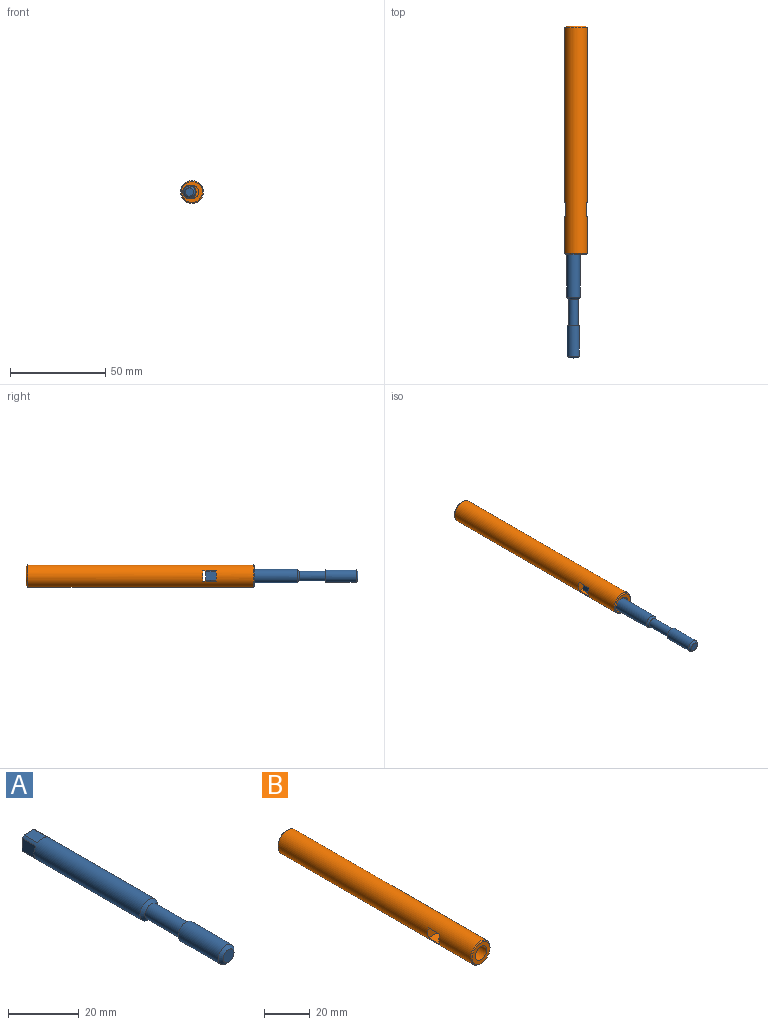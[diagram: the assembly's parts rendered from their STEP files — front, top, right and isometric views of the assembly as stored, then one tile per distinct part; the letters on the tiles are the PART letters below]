
ASSEMBLY  parts=2 mates=1
PART A: 16 faces, bbox 7x80x7 mm
  f0: cylinder r=3.5mm len=48mm, axis (0,1,0), area 958.9mm2, adj f1,f3,f8,f9,f10,f11,f12,f13
  f1: plane 5.82x5.5mm, normal (0,1,0), area 30.9mm2, adj f0,f9,f11,f13,f15
  f2: cylinder r=2.5mm len=14mm, axis (0,-1,0), area 219.9mm2, adj f3,f5
  f3: cone r=1.5mm half-angle=45deg, axis (0,1,0), area 26.7mm2, adj f0,f2
  f4: cylinder r=3.17mm len=16mm, axis (0,-1,0), area 319.2mm2, adj f5,f7
  f5: plane 6.35x6.35mm, normal (0,1,0), area 12mm2, adj f2,f4
  f6: plane 4.35x4.35mm, normal (0,-1,0), area 14.9mm2, adj f7
  f7: cone r=2.17mm half-angle=45deg, axis (0,1,0), area 23.8mm2, adj f4,f6
  f8: plane 3.89x0.59mm, normal (0,1,0), area 1.6mm2, adj f0,f9
  f9: plane 5.5x3.89mm, normal (0,0,1), area 21.4mm2, adj f0,f1,f8
  f10: plane 4.33x0.75mm, normal (0,1,0), area 2.2mm2, adj f0,f11
  f11: plane 5.5x4.33mm, normal (-1,0,0), area 23.8mm2, adj f0,f1,f10
  f12: plane 3.89x0.59mm, normal (0,1,0), area 1.6mm2, adj f0,f13
  f13: plane 5.5x3.89mm, normal (0,0,-1), area 21.4mm2, adj f0,f1,f12
  f14: plane 4.33x0.75mm, normal (0,1,0), area 2.2mm2, adj f0,f15
  f15: plane 5.5x4.33mm, normal (1,0,0), area 23.8mm2, adj f0,f1,f14
PART B: 13 faces, bbox 12x120x12 mm
  f0: plane 4.5x0.82mm, normal (0,-1,0), area 2.5mm2, adj f4,f12
  f1: cylinder r=6mm len=118.5mm, axis (0,1,0), area 4389.6mm2, adj f6,f7,f8,f9,f10,f11,f12
  f2: plane 11x11mm, normal (0,-1,0), area 56.5mm2, adj f4,f7
  f3: plane 10x10mm, normal (0,1,0), area 78.5mm2, adj f6
  f4: cylinder r=3.5mm len=20mm, axis (0,-1,0), area 439.8mm2, adj f0,f2,f5,f10,f11
  f5: plane 4.5x0.82mm, normal (0,-1,0), area 2.5mm2, adj f4,f9
  f6: cone r=6mm half-angle=45deg, axis (0,-1,0), area 48.9mm2, adj f1,f3
  f7: cone r=5.5mm half-angle=45deg, axis (0,1,0), area 25.5mm2, adj f1,f2
  f8: plane 12x5.36mm, normal (0,-1,0), area 62.1mm2, adj f1,f9,f12
  f9: plane 10.74x7mm, normal (0,0,-1), area 75.2mm2, adj f1,f5,f8,f10,f11
  f10: plane 5.36x3.75mm, normal (0,1,0), area 14.3mm2, adj f1,f4,f9,f12
  f11: plane 5.36x3.75mm, normal (0,1,0), area 14.3mm2, adj f1,f4,f9,f12
  f12: plane 10.74x7mm, normal (0,0,1), area 75.2mm2, adj f0,f1,f8,f10,f11
PLACE A t=(-49.89,2.19,-60.34)mm
PLACE B t=(-48.51,96.69,-60.34)mm
MATE planar A.f10 <-> B.f10  axis (0,1,0) through (-52.95,-3.31,-60.34)mm
